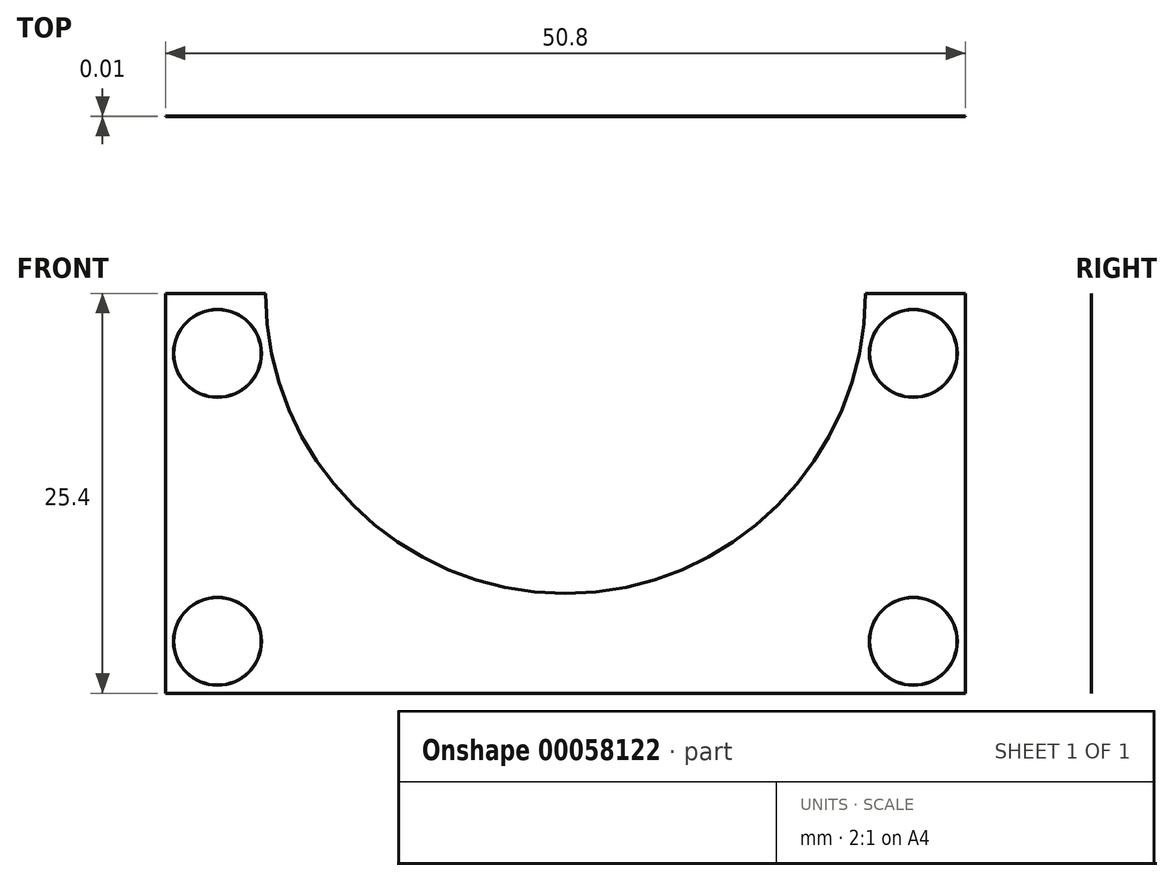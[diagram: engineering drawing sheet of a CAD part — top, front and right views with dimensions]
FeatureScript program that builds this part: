
annotation { "Feature Type Name" : "Feature", "Feature Type Description" : "" }
export const myFeature = defineFeature(function(context is Context, id is Id, definition is map)
    precondition{}
    {
        {
            var Q0;
            Q0=qCreatedBy(makeId("Front.planeOp"),FACE);
            var sketch = newSketch(context, id + "F0", { "sketchPlane" : qUnion([Q0])});
            skLineSegment(sketch, "E0.rect.top", {"start": v(-25.4, -12.7) * mm, "end": v(25.4, -12.7) * mm});
            skLineSegment(sketch, "E0.rect.left", {"start": v(-25.4, 12.7) * mm, "end": v(-25.4, -12.7) * mm});
            skLineSegment(sketch, "E0.rect.right", {"start": v(25.4, 12.7) * mm, "end": v(25.4, -12.7) * mm});
            skPoint(sketch, "E0.rect.middle", {"position": v(0, 0) * mm});
            skArc(sketch, "E1", {"start": v(-19.05, 12.7) * mm, "mid": v(0, -6.35) * mm, "end": v(19.05, 12.7) * mm});
            skLineSegment(sketch, "E2", {"start": v(25.4, 12.7) * mm, "end": v(19.05, 12.7) * mm});
            skLineSegment(sketch, "E3", {"start": v(-19.05, 12.7) * mm, "end": v(-25.4, 12.7) * mm});
            skLineSegment(sketch, "E4", {"start": v(-25.4, 12.7) * mm, "end": v(25.4, 12.7) * mm, "construction": true});
            skLineSegment(sketch, "E5.0", {"start": v(22.1, 12.7) * mm, "end": v(22.1, -9.4) * mm, "construction": true});
            skLineSegment(sketch, "E5.1", {"start": v(-22.1, -9.4) * mm, "end": v(22.1, -9.4) * mm, "construction": true});
            skLineSegment(sketch, "E5.2", {"start": v(-22.1, 12.7) * mm, "end": v(-22.1, -9.4) * mm, "construction": true});
            skLineSegment(sketch, "E6", {"start": v(-22.1, 8.9) * mm, "end": v(22.1, 8.9) * mm, "construction": true});
            skCircle(sketch, "E7", {"center": v(-22.1, 8.9) * mm, "radius": 2.03 * mm});
            skCircle(sketch, "E8", {"center": v(-22.1, -9.4) * mm, "radius": 2.03 * mm});
            skCircle(sketch, "E9", {"center": v(22.1, -9.4) * mm, "radius": 2.03 * mm});
            skCircle(sketch, "E10", {"center": v(22.1, 8.9) * mm, "radius": 2.03 * mm});
            skSolve(sketch);
        }
        {
            var Q0;
            Q0=makeQuery(id+"F0.imprint","IMPRINT",FACE,{"disambiguationData":[TD([[makeQuery(id+"F0.imprint","IMPRINT",EDGE,{"derivedFrom":sQuery(id+"F0.wireOp",EDGE,"E0.rect.top")}),1.0]])]});
            extrude(context, id + "F1", {"entities" : qUnion([Q0]), "depth" : 9 / 645.16 * mm});
        }
        {
            var Q0;
            Q0=makeQuery(id+"F1.opExtrude","CAP_EDGE",EDGE,{"disambiguationData":[OSD([sQuery(id+"F0.wireOp",EDGE,"E7")])],"isStart":false});
            var Q1;
            Q1=makeQuery(id+"F1.opExtrude","CAP_EDGE",EDGE,{"disambiguationData":[OSD([sQuery(id+"F0.wireOp",EDGE,"E8")])],"isStart":false});
            var Q2;
            Q2=makeQuery(id+"F1.opExtrude","CAP_EDGE",EDGE,{"disambiguationData":[OSD([sQuery(id+"F0.wireOp",EDGE,"E9")])],"isStart":false});
            var Q3;
            Q3=makeQuery(id+"F1.opExtrude","CAP_EDGE",EDGE,{"disambiguationData":[OSD([sQuery(id+"F0.wireOp",EDGE,"E10")])],"isStart":false});
            chamfer(context, id + "F2", {"entities" : qUnion([Q0, Q1, Q2, Q3]), "width" : 0.76 * mm, "tangentPropagation" : true});
        }
    });
